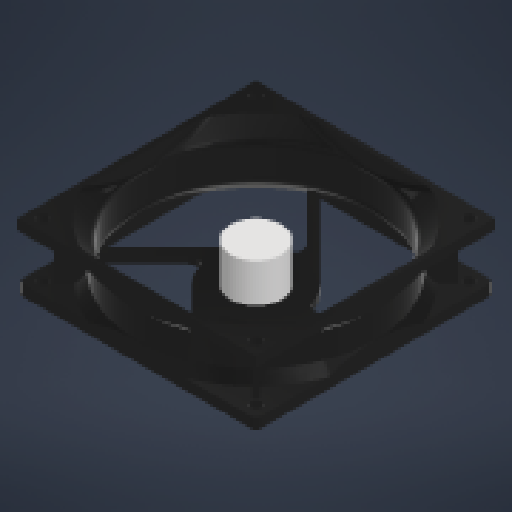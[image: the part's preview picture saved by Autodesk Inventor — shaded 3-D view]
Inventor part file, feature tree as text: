
AUTODESK INVENTOR PART (.ipt)
format: ipt  version: 2024 (Build 280153000, 153)  size: 960,000 bytes
history: native  units: mm
features: extrude x10, projected_geometry x8, sketch x7, fillet x4, chamfer x3, other x2
ambient origin geometry x8: Origin, YZ Plane, XZ Plane, XY Plane, X Axis, Y Axis, Z Axis, Center Point
bodies: Body1 (feature_tree)
feature tree (34):
  other  "솔리드1"
  sketch  "스케치1"
  extrude  "돌출1"  Depth=92.0mm
  extrude  "돌출2"  Depth=92.0mm
  sketch  "스케치3"
  extrude  "돌출3"  Depth=4.0mm
  sketch  "스케치4"
  extrude  "돌출4"  Depth=4.0mm
  fillet  "모깎기1"  Radius=4.0mm
  fillet  "모깎기2"  Radius=4.0mm
  chamfer  "모따기1"  Distance=82.0mm
  chamfer  "모따기2"  Distance=82.0mm
  extrude  "돌출5"  Depth=5.0mm
  extrude  "돌출6"  Depth=5.0mm
  chamfer  "모따기3"  Distance=5.0mm
  extrude  "돌출7"  Depth=5.0mm
  extrude  "돌출8"  Depth=5.0mm
  fillet  "모깎기3"  Radius=4.0mm
  extrude  "돌출9"  Depth=88.0mm
  fillet  "모깎기4"  Radius=2.0mm
  extrude  "돌출10"  Depth=9.0mm
  sketch  "스케치2"
  sketch  "스케치6"
  projected_geometry  "투영된 루프1"
  projected_geometry  "투영된 루프2"
  projected_geometry  "투영된 루프3"
  projected_geometry  "투영된 루프4"
  sketch  "스케치7"
  projected_geometry  "투영된 루프5"
  projected_geometry  "투영된 루프6"
  projected_geometry  "투영된 루프7"
  projected_geometry  "투영된 루프8"
  sketch  "스케치8"
  other  "Finish1"
